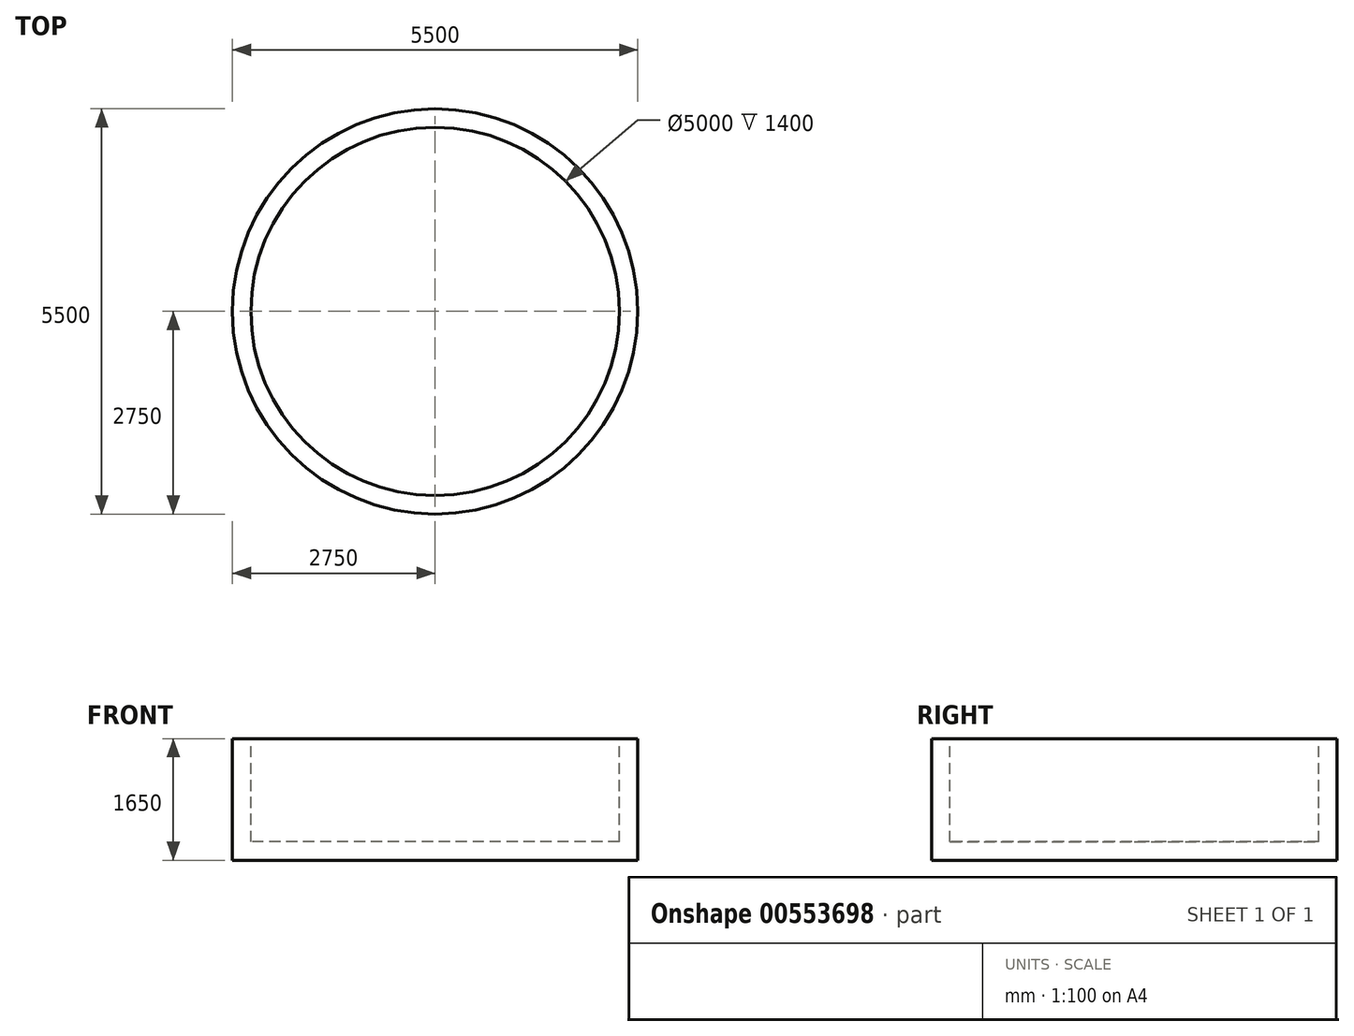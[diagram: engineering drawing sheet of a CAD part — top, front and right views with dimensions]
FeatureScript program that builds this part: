
annotation { "Feature Type Name" : "Feature", "Feature Type Description" : "" }
export const myFeature = defineFeature(function(context is Context, id is Id, definition is map)
    precondition{}
    {
        {
            var Q0;
            Q0=qCreatedBy(makeId("Top.planeOp"),FACE);
            var sketch = newSketch(context, id + "F0", { "sketchPlane" : qUnion([Q0])});
            skLineSegment(sketch, "E0.bottom", {"start": v(2750, -2750) * mm, "end": v(-2750, -2750) * mm});
            skLineSegment(sketch, "E0.top", {"start": v(2750, 2750) * mm, "end": v(-2750, 2750) * mm});
            skLineSegment(sketch, "E0.left", {"start": v(2750, -2750) * mm, "end": v(2750, 2750) * mm});
            skLineSegment(sketch, "E0.right", {"start": v(-2750, -2750) * mm, "end": v(-2750, 2750) * mm});
            skPoint(sketch, "E0.middle", {"position": v(0, 0) * mm});
            skSolve(sketch);
        }
        {
            var Q0;
            Q0 = qSketchRegion(id + "F0", true);
            extrude(context, id + "F1", {"entities" : qUnion([Q0]), "depth" : 1650 * mm, "offsetDistance" : 25 * mm});
        }
        {
            var Q0;
            Q0=makeQuery(id+"F1.opExtrude","SWEPT_EDGE",EDGE,{"disambiguationData":[OSD([sQuery(id+"F0.wireOp",EDGE,"E0.bottom"),sQuery(id+"F0.wireOp",EDGE,"E0.right")])]});
            var Q1;
            Q1=makeQuery(id+"F1.opExtrude","SWEPT_EDGE",EDGE,{"disambiguationData":[OSD([sQuery(id+"F0.wireOp",EDGE,"E0.bottom"),sQuery(id+"F0.wireOp",EDGE,"E0.left")])]});
            var Q2;
            Q2=makeQuery(id+"F1.opExtrude","SWEPT_EDGE",EDGE,{"disambiguationData":[OSD([sQuery(id+"F0.wireOp",EDGE,"E0.top"),sQuery(id+"F0.wireOp",EDGE,"E0.left")])]});
            var Q3;
            Q3=makeQuery(id+"F1.opExtrude","SWEPT_EDGE",EDGE,{"disambiguationData":[OSD([sQuery(id+"F0.wireOp",EDGE,"E0.top"),sQuery(id+"F0.wireOp",EDGE,"E0.right")])]});
            fillet(context, id + "F2", {"entities" : qUnion([Q0, Q1, Q2, Q3]), "radius" : 2750 * mm, "tangentPropagation" : true, "allowEdgeOverflow" : false});
        }
        {
            var Q0;
            Q0=makeQuery(id+"F1.opExtrude","CAP_FACE",FACE,{"disambiguationData":[OSD([sQuery(id+"F0.wireOp",EDGE,"E0.bottom"),sQuery(id+"F0.wireOp",EDGE,"E0.top"),sQuery(id+"F0.wireOp",EDGE,"E0.left"),sQuery(id+"F0.wireOp",EDGE,"E0.right")])],"isStart":false});
            shell(context, id + "F3", {"entities" : qUnion([Q0]), "thickness" : 250 * mm});
        }
    });
